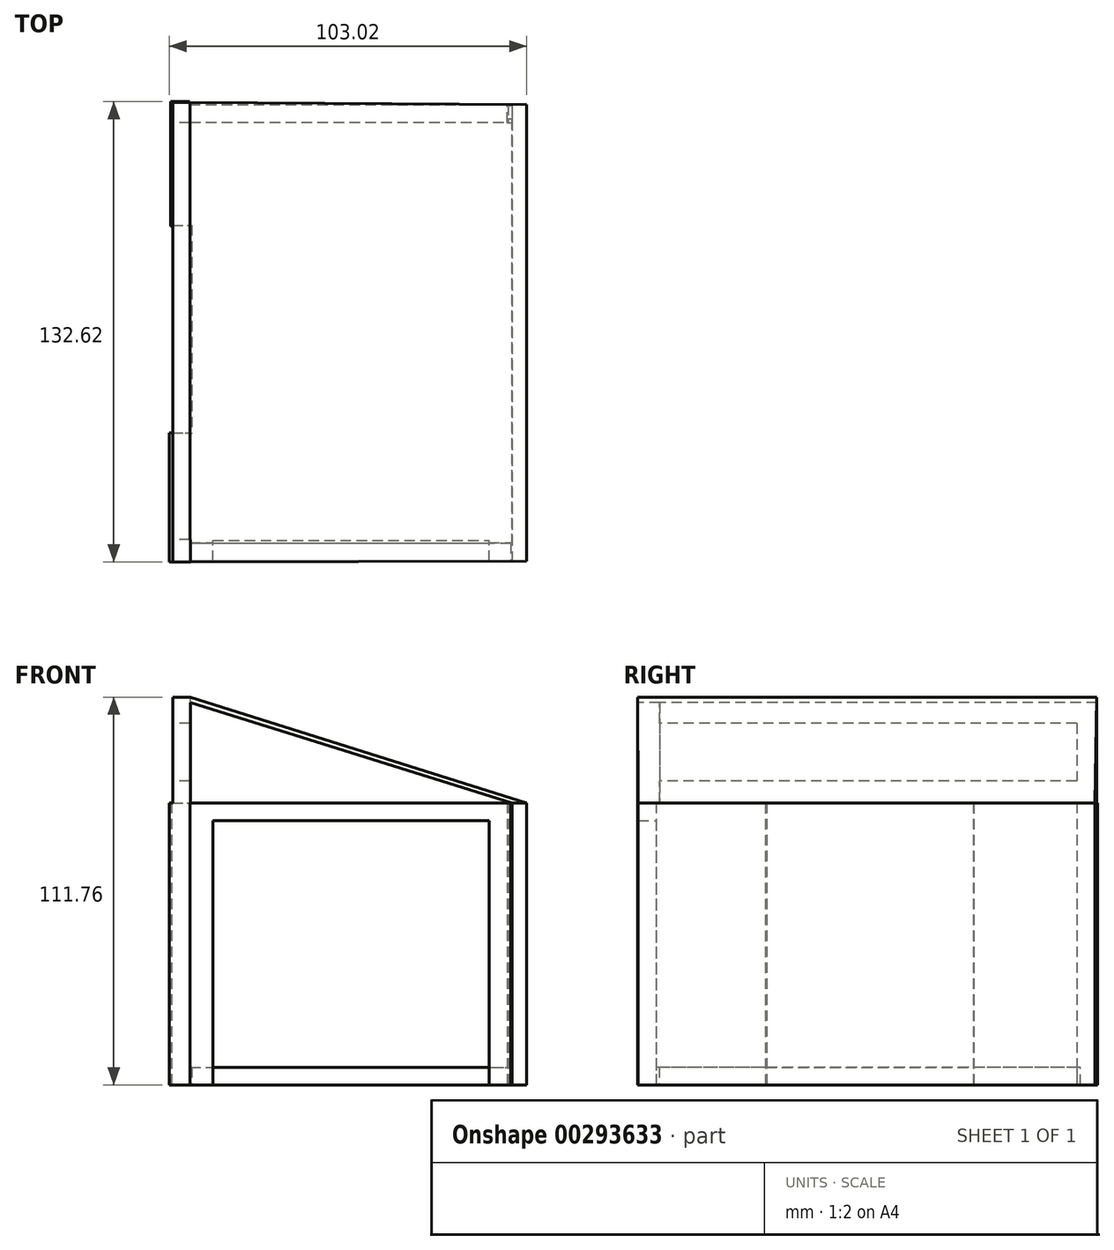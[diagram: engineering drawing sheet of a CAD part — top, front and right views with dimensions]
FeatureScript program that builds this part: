
annotation { "Feature Type Name" : "Feature", "Feature Type Description" : "" }
export const myFeature = defineFeature(function(context is Context, id is Id, definition is map)
    precondition{}
    {
        {
            var Q0;
            Q0=qCreatedBy(makeId("Top.planeOp"),FACE);
            var sketch = newSketch(context, id + "F0", { "sketchPlane" : qUnion([Q0])});
            skLineSegment(sketch, "E0.bottom", {"start": v(-45.87, 59.12) * mm, "end": v(45.87, 59.12) * mm});
            skLineSegment(sketch, "E0.top", {"start": v(-45.87, 54.02) * mm, "end": v(45.87, 54.02) * mm});
            skLineSegment(sketch, "E0.left", {"start": v(-45.87, 59.12) * mm, "end": v(-45.87, 54.02) * mm});
            skLineSegment(sketch, "E0.right", {"start": v(45.87, 59.12) * mm, "end": v(45.87, 54.02) * mm});
            skPoint(sketch, "E0.middle", {"position": v(0, 56.57) * mm});
            skSolve(sketch);
        }
        {
            var Q0;
            Q0 = qSketchRegion(id + "F0", true);
            extrude(context, id + "F1", {"entities" : qUnion([Q0]), "depth" : 81.28 * mm});
        }
        {
            var Q0;
            Q0=qCreatedBy(makeId("Top.planeOp"),FACE);
            var sketch = newSketch(context, id + "F2", { "sketchPlane" : qUnion([Q0])});
            skLineSegment(sketch, "E1.bottom", {"start": v(-45.81, 55.03) * mm, "end": v(46.95, 55.03) * mm});
            skLineSegment(sketch, "E1.top", {"start": v(-45.81, -67.14) * mm, "end": v(46.95, -67.14) * mm});
            skLineSegment(sketch, "E1.left", {"start": v(-45.81, 55.03) * mm, "end": v(-45.81, -67.14) * mm});
            skLineSegment(sketch, "E1.right", {"start": v(46.95, 55.03) * mm, "end": v(46.95, -67.14) * mm});
            skSolve(sketch);
        }
        {
            var Q0;
            Q0 = qSketchRegion(id + "F2", true);
            extrude(context, id + "F3", {"entities" : qUnion([Q0]), "operationType" : NewBodyOperationType.ADD, "depth" : 5.08 * mm});
        }
        {
            var Q0;
            Q0=qCreatedBy(makeId("Top.planeOp"),FACE);
            var sketch = newSketch(context, id + "F4", { "sketchPlane" : qUnion([Q0])});
            skLineSegment(sketch, "E2.bottom", {"start": v(46.6, -67.36) * mm, "end": v(-45.8, -67.36) * mm});
            skLineSegment(sketch, "E2.top", {"start": v(46.6, -72.45) * mm, "end": v(-45.8, -72.45) * mm});
            skLineSegment(sketch, "E2.left", {"start": v(46.6, -67.36) * mm, "end": v(46.6, -72.45) * mm});
            skLineSegment(sketch, "E2.right", {"start": v(-45.8, -67.36) * mm, "end": v(-45.8, -72.45) * mm});
            skSolve(sketch);
        }
        {
            var Q0;
            Q0 = qSketchRegion(id + "F4", true);
            extrude(context, id + "F5", {"entities" : qUnion([Q0]), "depth" : 81.28 * mm});
        }
        {
            var Q0;
            Q0=qCreatedBy(makeId("Top.planeOp"),FACE);
            var sketch = newSketch(context, id + "F6", { "sketchPlane" : qUnion([Q0])});
            skLineSegment(sketch, "E3.bottom", {"start": v(47.01, 59.18) * mm, "end": v(51.2, 59.18) * mm});
            skLineSegment(sketch, "E3.top", {"start": v(47.01, -72.51) * mm, "end": v(51.2, -72.51) * mm});
            skLineSegment(sketch, "E3.left", {"start": v(47.01, 59.18) * mm, "end": v(47.01, -72.51) * mm});
            skLineSegment(sketch, "E3.right", {"start": v(51.2, 59.18) * mm, "end": v(51.2, -72.51) * mm});
            skSolve(sketch);
        }
        {
            var Q0;
            Q0=makeQuery(id+"F6.imprint","IMPRINT",FACE,{"disambiguationData":[TD([[makeQuery(id+"F6.imprint","IMPRINT",EDGE,{"derivedFrom":sQuery(id+"F6.wireOp",EDGE,"E3.bottom")}),-1.0]])]});
            extrude(context, id + "F7", {"entities" : qUnion([Q0]), "depth" : 81.28 * mm});
        }
        {
            var Q0;
            Q0=qCreatedBy(makeId("Top.planeOp"),FACE);
            var sketch = newSketch(context, id + "F8", { "sketchPlane" : qUnion([Q0])});
            skLineSegment(sketch, "E4.bottom", {"start": v(45.63, 53.93) * mm, "end": v(47.2, 53.93) * mm});
            skLineSegment(sketch, "E4.top", {"start": v(45.63, 58.9) * mm, "end": v(47.2, 58.9) * mm});
            skLineSegment(sketch, "E4.left", {"start": v(45.63, 53.93) * mm, "end": v(45.63, 58.9) * mm});
            skLineSegment(sketch, "E4.right", {"start": v(47.2, 53.93) * mm, "end": v(47.2, 58.9) * mm});
            skSolve(sketch);
        }
        {
            var Q0;
            Q0 = qSketchRegion(id + "F8", true);
            extrude(context, id + "F9", {"entities" : qUnion([Q0]), "depth" : 81.28 * mm});
        }
        {
            var Q0;
            Q0=qCreatedBy(makeId("Top.planeOp"),FACE);
            var sketch = newSketch(context, id + "F10", { "sketchPlane" : qUnion([Q0])});
            skLineSegment(sketch, "E5.bottom", {"start": v(-45.85, 59.75) * mm, "end": v(-50.82, 59.75) * mm});
            skLineSegment(sketch, "E5.top", {"start": v(-45.85, -72.65) * mm, "end": v(-50.82, -72.65) * mm});
            skLineSegment(sketch, "E5.left", {"start": v(-45.85, 59.75) * mm, "end": v(-45.85, -72.65) * mm});
            skLineSegment(sketch, "E5.right", {"start": v(-50.82, 59.75) * mm, "end": v(-50.82, -72.65) * mm});
            skSolve(sketch);
        }
        {
            var Q0;
            Q0 = qSketchRegion(id + "F10", true);
            extrude(context, id + "F11", {"entities" : qUnion([Q0]), "operationType" : NewBodyOperationType.ADD, "depth" : 111.76 * mm});
        }
        {
            var Q0;
            Q0=makeQuery(id+"F11.opExtrude","CAP_FACE",FACE,{"disambiguationData":[OSD([sQuery(id+"F10.wireOp",EDGE,"E5.bottom"),sQuery(id+"F10.wireOp",EDGE,"E5.top"),sQuery(id+"F10.wireOp",EDGE,"E5.left"),sQuery(id+"F10.wireOp",EDGE,"E5.right")])],"isStart":false});
            var Q1;
            Q1=makeQuery(id+"F7.opExtrude","CAP_FACE",FACE,{"disambiguationData":[OSD([sQuery(id+"F6.wireOp",EDGE,"E3.bottom"),sQuery(id+"F6.wireOp",EDGE,"E3.top"),sQuery(id+"F6.wireOp",EDGE,"E3.left"),sQuery(id+"F6.wireOp",EDGE,"E3.right")])],"isStart":false});
            loft(context, id + "F12", {"sheetProfilesArray" : [{ "sheetProfileEntities" : qUnion([Q0]) }, { "sheetProfileEntities" : qUnion([Q1]) }]});
        }
        {
            var Q0;
            Q0=qCreatedBy(makeId("Top.planeOp"),FACE);
            var sketch = newSketch(context, id + "F13", { "sketchPlane" : qUnion([Q0])});
            skLineSegment(sketch, "E6.bottom", {"start": v(-51.36, 59.97) * mm, "end": v(-45.95, 59.97) * mm});
            skLineSegment(sketch, "E6.top", {"start": v(-51.36, 24.1) * mm, "end": v(-45.95, 24.1) * mm});
            skLineSegment(sketch, "E6.left", {"start": v(-51.36, 59.97) * mm, "end": v(-51.36, 24.1) * mm});
            skLineSegment(sketch, "E6.right", {"start": v(-45.95, 59.97) * mm, "end": v(-45.95, 24.1) * mm});
            skSolve(sketch);
        }
        {
            var Q0;
            Q0 = qSketchRegion(id + "F13", true);
            extrude(context, id + "F14", {"entities" : qUnion([Q0]), "operationType" : NewBodyOperationType.ADD, "depth" : 81.28 * mm});
        }
        {
            var Q0;
            Q0=qCreatedBy(makeId("Top.planeOp"),FACE);
            var sketch = newSketch(context, id + "F15", { "sketchPlane" : qUnion([Q0])});
            skLineSegment(sketch, "E7.bottom", {"start": v(-51.14, 24.34) * mm, "end": v(-45.27, 24.34) * mm});
            skLineSegment(sketch, "E7.top", {"start": v(-51.14, -35.66) * mm, "end": v(-45.27, -35.66) * mm});
            skLineSegment(sketch, "E7.left", {"start": v(-51.14, 24.34) * mm, "end": v(-51.14, -35.66) * mm});
            skLineSegment(sketch, "E7.right", {"start": v(-45.27, 24.34) * mm, "end": v(-45.27, -35.66) * mm});
            skSolve(sketch);
        }
        {
            var Q0;
            Q0 = qSketchRegion(id + "F15", true);
            extrude(context, id + "F16", {"entities" : qUnion([Q0]), "operationType" : NewBodyOperationType.REMOVE, "depth" : 81.28 * mm});
        }
        {
            var Q0;
            Q0=qCreatedBy(makeId("Top.planeOp"),FACE);
            var sketch = newSketch(context, id + "F17", { "sketchPlane" : qUnion([Q0])});
            skLineSegment(sketch, "E8.bottom", {"start": v(-51.81, -35.44) * mm, "end": v(-45.95, -35.44) * mm});
            skLineSegment(sketch, "E8.top", {"start": v(-51.81, -72.65) * mm, "end": v(-45.95, -72.65) * mm});
            skLineSegment(sketch, "E8.left", {"start": v(-51.81, -35.44) * mm, "end": v(-51.81, -72.65) * mm});
            skLineSegment(sketch, "E8.right", {"start": v(-45.95, -35.44) * mm, "end": v(-45.95, -72.65) * mm});
            skSolve(sketch);
        }
        {
            var Q0;
            Q0 = qSketchRegion(id + "F17", true);
            extrude(context, id + "F18", {"entities" : qUnion([Q0]), "operationType" : NewBodyOperationType.ADD, "depth" : 81.28 * mm});
        }
        {
            var Q0;
            Q0=qCreatedBy(makeId("Top.planeOp"),FACE);
            var sketch = newSketch(context, id + "F19", { "sketchPlane" : qUnion([Q0])});
            skLineSegment(sketch, "E9.bottom", {"start": v(-39.22, -73.02) * mm, "end": v(40.4, -73.02) * mm});
            skLineSegment(sketch, "E9.top", {"start": v(-39.22, -66.47) * mm, "end": v(40.4, -66.47) * mm});
            skLineSegment(sketch, "E9.left", {"start": v(-39.22, -73.02) * mm, "end": v(-39.22, -66.47) * mm});
            skLineSegment(sketch, "E9.right", {"start": v(40.4, -73.02) * mm, "end": v(40.4, -66.47) * mm});
            skSolve(sketch);
        }
        {
            var Q0;
            Q0 = qSketchRegion(id + "F19", true);
            extrude(context, id + "F20", {"entities" : qUnion([Q0]), "operationType" : NewBodyOperationType.REMOVE, "depth" : 76.2 * mm});
        }
        {
            var Q0;
            Q0=makeQuery(id+"F11.opExtrude","SWEPT_FACE",FACE,{"disambiguationData":[OSD([sQuery(id+"F10.wireOp",EDGE,"E5.right")])]});
            var sketch = newSketch(context, id + "F21", { "sketchPlane" : qUnion([Q0])});
            skLineSegment(sketch, "E10.bottom", {"start": v(-53.94, 104.22) * mm, "end": v(66.24, 104.22) * mm});
            skLineSegment(sketch, "E10.top", {"start": v(-53.94, 87.52) * mm, "end": v(66.24, 87.52) * mm});
            skLineSegment(sketch, "E10.left", {"start": v(-53.94, 104.22) * mm, "end": v(-53.94, 87.52) * mm});
            skLineSegment(sketch, "E10.right", {"start": v(66.24, 104.22) * mm, "end": v(66.24, 87.52) * mm});
            skSolve(sketch);
        }
        {
            var Q0;
            Q0 = qSketchRegion(id + "F21", true);
            extrude(context, id + "F22", {"entities" : qUnion([Q0]), "operationType" : NewBodyOperationType.REMOVE, "oppositeDirection" : true, "depth" : 7.62 * mm});
        }
        {
            var Q0;
            Q0=makeQuery(id+"F11.opExtrude","SWEPT_FACE",FACE,{"disambiguationData":[OSD([sQuery(id+"F10.wireOp",EDGE,"E5.right")])]});
            var sketch = newSketch(context, id + "F23", { "sketchPlane" : qUnion([Q0])});
            skLineSegment(sketch, "E11.bottom", {"start": v(66.24, 111.76) * mm, "end": v(72.65, 111.76) * mm});
            skLineSegment(sketch, "E11.top", {"start": v(66.24, 81.28) * mm, "end": v(72.65, 81.28) * mm});
            skLineSegment(sketch, "E11.left", {"start": v(66.24, 111.76) * mm, "end": v(66.24, 81.28) * mm});
            skLineSegment(sketch, "E11.right", {"start": v(72.65, 111.76) * mm, "end": v(72.65, 81.28) * mm});
            skSolve(sketch);
        }
        {
            var Q0;
            Q0 = qSketchRegion(id + "F23", true);
            extrude(context, id + "F24", {"entities" : qUnion([Q0]), "operationType" : NewBodyOperationType.ADD, "oppositeDirection" : true, "depth" : 5.08 * mm});
        }
    });
